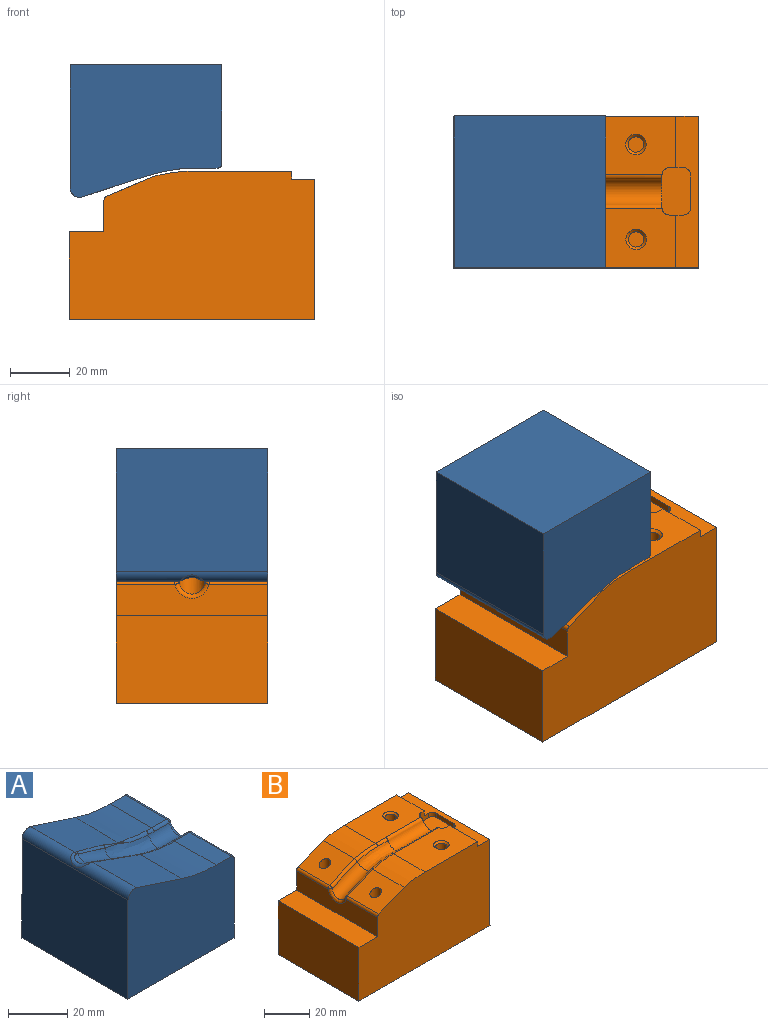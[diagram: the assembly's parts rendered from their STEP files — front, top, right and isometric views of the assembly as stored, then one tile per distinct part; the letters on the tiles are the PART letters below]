
ASSEMBLY  parts=2 mates=1
PART A: 34 faces, bbox 57.8x52.3x48.8 mm
  f0: plane 21.63x21.13mm, normal (0.31,0,0.95), area 465.5mm2, adj f1,f9,f12,f20,f22,f24
  f1: cylinder r=53.34mm len=19.96mm, axis (0,1,0), area 333.5mm2, adj f0,f7,f9,f18,f19
  f2: plane 19.91x7.27mm, normal (0,0,1), area 144.7mm2, adj f6,f10,f13,f29
  f3: plane 50.8x50.8mm, normal (0,0,-1), area 2580.6mm2, adj f4,f8,f9,f10
  f4: plane 50.8x41.16mm, normal (-1,0,0), area 2091mm2, adj f3,f9,f10,f12
  f5: plane 23.15x22.68mm, normal (0.31,0,0.95), area 466.2mm2, adj f6,f10,f12,f28,f30,f32
  f6: cylinder r=53.34mm len=19.99mm, axis (0,1,0), area 334mm2, adj f2,f5,f10,f31,f33
  f7: plane 19.89x7.27mm, normal (0,0,1), area 144.5mm2, adj f1,f9,f14,f21
  f8: plane 50.8x33.27mm, normal (1,0,0), area 1658.3mm2, adj f3,f9,f10,f13,f14,f25
  f9: plane 50.8x44.34mm, normal (0,-1,0), area 1939.6mm2, adj f0,f1,f3,f4,f7,f8,f12,f14
  f10: plane 50.8x44.34mm, normal (0,1,0), area 1939.6mm2, adj f2,f3,f4,f5,f6,f8,f12,f13
  f11: cylinder r=4.52mm len=6.64mm, axis (0.95,0,-0.31), area 18.4mm2, adj f17,f22,f24,f26,f28,f30
  f12: cylinder r=3.17mm len=50.8mm, axis (0,-1,0), area 271.3mm2, adj f0,f4,f5,f9,f10,f26
  f13: cylinder r=1.27mm len=19.91mm, axis (0,-1,0), area 39.7mm2, adj f2,f8,f10,f27
  f14: cylinder r=1.27mm len=19.89mm, axis (0,-1,0), area 39.7mm2, adj f7,f8,f9,f23
  f15: cylinder r=4.52mm len=10.03mm, axis (-1,0,0), area 113.7mm2, adj f16,f19,f21,f25,f29,f31
  f16: bspline ~24x14.71mm, area 247.5mm2, adj f15,f17,f18,f19,f20,f31,f32,f33
  f17: cylinder r=4.52mm len=14.19mm, axis (-0.92,0,0.39), area 124.7mm2, adj f11,f16,f20,f22,f30
  f18: bspline ~18.74x4.92mm, area 22.2mm2, adj f1,f16,f19,f20
  f19: bspline ~7.78x1.25mm, area 4.4mm2, adj f1,f15,f16,f18,f21
  f20: bspline ~12.13x4.67mm, area 11.2mm2, adj f0,f16,f17,f18,f22
  f21: cylinder r=1.27mm len=7.27mm, axis (-1,0,0), area 11.6mm2, adj f7,f15,f19,f23
  f22: bspline ~31.18x10.92mm, area 17.7mm2, adj f0,f11,f17,f20,f24
  f23: sphere r=1.27mm, area 3.1mm2, adj f14,f21,f25
  f24: bspline ~14.81x5.16mm, area 0.9mm2, adj f0,f11,f22,f26
  f25: torus R=5.79mm, axis (1,0,0), area 24.9mm2, adj f8,f15,f23,f27
  f26: bspline ~8.5x4.36mm, area 17.4mm2, adj f11,f12,f24,f28
  f27: sphere r=1.27mm, area 1.2mm2, adj f13,f25,f29
  f28: bspline ~14.81x5.16mm, area 0.9mm2, adj f5,f11,f26,f30
  f29: cylinder r=1.27mm len=7.27mm, axis (-1,0,0), area 11.6mm2, adj f2,f15,f27,f31
  f30: bspline ~13.79x5.13mm, area 17.7mm2, adj f5,f11,f17,f28,f32
  f31: bspline ~7.78x1.25mm, area 4.4mm2, adj f6,f15,f16,f29,f33
  f32: bspline ~9.06x3.7mm, area 5.6mm2, adj f5,f16,f30
  f33: bspline ~16.51x4.08mm, area 22.2mm2, adj f6,f16,f31
PART B: 53 faces, bbox 86.6x55.2x53.9 mm
  f0: cylinder r=50.8mm len=19.81mm, axis (0,-1,0), area 263.6mm2, adj f1,f7,f34,f50
  f1: plane 82.24x49.53mm, normal (0,-1,0), area 3720.5mm2, adj f0,f3,f7,f9,f11,f12,f13,f14
  f2: plane 82.1x49.53mm, normal (0,1,0), area 3713.9mm2, adj f3,f4,f8,f9,f10,f11,f12,f13
  f3: plane 50.82x10.49mm, normal (-1,0,0), area 494.3mm2, adj f1,f2,f14,f43,f46,f47
  f4: cylinder r=50.8mm len=19.8mm, axis (0,-1,0), area 263.5mm2, adj f2,f8,f35,f42
  f5: bspline ~19.41x8.63mm, area 206.2mm2, adj f6,f33,f41,f42,f44,f49,f50,f51
  f6: cylinder r=4.52mm len=16.78mm, axis (-0.92,0,-0.39), area 193.3mm2, adj f5,f44,f47,f49
  f7: plane 33x19.82mm, normal (0,0,1), area 605.9mm2, adj f0,f1,f15,f18,f24,f30,f51,f52
  f8: plane 33x19.82mm, normal (0,0,1), area 604.1mm2, adj f2,f4,f10,f16,f21,f29,f40,f41
  f9: plane 50.82x7.75mm, normal (0,0,1), area 313.1mm2, adj f1,f2,f10,f11,f15,f16,f17,f18
  f10: plane 17.31x2.67mm, normal (1,0,0), area 46.2mm2, adj f2,f8,f9,f16
  f11: plane 50.82x46.87mm, normal (1,0,0), area 2368.9mm2, adj f1,f2,f9,f13,f31
  f12: plane 50.82x29.21mm, normal (-1,0,0), area 1484.5mm2, adj f1,f2,f13,f14
  f13: plane 82.24x50.82mm, normal (0,0,-1), area 4175.9mm2, adj f1,f2,f11,f12
  f14: plane 50.82x11.62mm, normal (0,0,1), area 590.8mm2, adj f1,f2,f3,f12
  f15: plane 17.68x2.67mm, normal (1,0,0), area 47.2mm2, adj f1,f7,f9,f18
  f16: plane 4.99x4.79mm, normal (0,-1,0), area 16.9mm2, adj f8,f9,f10,f20,f21,f22
  f17: plane 11x2.32mm, normal (-1,0,0), area 25.6mm2, adj f9,f20,f22,f23
  f18: plane 4.99x4.79mm, normal (0,1,0), area 16.9mm2, adj f7,f9,f15,f20,f23,f24
  f19: plane 11x4.99mm, normal (1,0,0), area 27mm2, adj f20,f21,f24,f33,f40,f52
  f20: plane 15.83x9.62mm, normal (0,0,1), area 147.2mm2, adj f16,f17,f18,f19,f21,f22,f23,f24
  f21: cylinder r=2.41mm len=4.99mm, axis (0,0,1), area 18.9mm2, adj f8,f16,f19,f20,f40
  f22: cylinder r=2.41mm len=2.41mm, axis (0,0,-1), area 8.8mm2, adj f9,f16,f17,f20
  f23: cylinder r=2.41mm len=2.41mm, axis (0,0,1), area 8.8mm2, adj f9,f17,f18,f20
  f24: cylinder r=2.41mm len=4.99mm, axis (0,0,-1), area 18.9mm2, adj f7,f18,f19,f20,f52
  f25: cylinder r=2.55mm len=18.16mm, axis (0,0,1), area 291.3mm2, adj f26,f30
  f26: plane 5.11x5.11mm, normal (0,0,1), area 20.5mm2, adj f25
  f27: cylinder r=2.55mm len=18.16mm, axis (0,0,1), area 291.3mm2, adj f28,f29
  f28: plane 5.11x5.11mm, normal (0,0,1), area 20.5mm2, adj f27
  f29: cone r=2.55mm half-angle=45deg, axis (0,0,1), area 23.7mm2, adj f8,f27
  f30: cone r=2.55mm half-angle=45deg, axis (0,0,1), area 23.7mm2, adj f7,f25
  f31: cylinder r=2.02mm len=19.06mm, axis (1,0,0), area 241.7mm2, adj f11,f32
  f32: plane 4.04x4.04mm, normal (1,0,0), area 12.8mm2, adj f31
  f33: cylinder r=4.52mm len=21.98mm, axis (-1,0,0), area 243.5mm2, adj f5,f19,f40,f41,f51,f52
  f34: plane 23.98x20.07mm, normal (-0.39,0,0.92), area 313.6mm2, adj f0,f1,f37,f46,f49,f50
  f35: plane 23.98x20.07mm, normal (-0.39,0,0.92), area 313.5mm2, adj f2,f4,f39,f42,f43,f44
  f36: plane 5.11x5.11mm, normal (0,0,1), area 20.5mm2, adj f37
  f37: cylinder r=2.55mm len=21.21mm, axis (0,0,1), area 340.2mm2, adj f34,f36
  f38: plane 5.11x5.11mm, normal (0,0,1), area 20.5mm2, adj f39
  f39: cylinder r=2.55mm len=21.17mm, axis (0,0,1), area 339.6mm2, adj f35,f38
  f40: cylinder r=1.52mm len=22mm, axis (-1,0,0), area 41.1mm2, adj f8,f19,f21,f33,f41
  f41: bspline ~12.12x1.56mm, area 11.7mm2, adj f5,f8,f33,f40,f42
  f42: bspline ~18.43x3.09mm, area 24.8mm2, adj f4,f5,f35,f41,f44
  f43: cylinder r=1.52mm len=19.64mm, axis (0,1,0), area 35mm2, adj f2,f3,f35,f45
  f44: cylinder r=1.52mm len=16.15mm, axis (-0.92,0,-0.39), area 32.9mm2, adj f5,f6,f35,f42,f45
  f45: sphere r=1.52mm, area 1.7mm2, adj f43,f44,f47
  f46: cylinder r=1.52mm len=19.65mm, axis (0,1,0), area 35mm2, adj f1,f3,f34,f48
  f47: bspline ~11.53x5.01mm, area 26.5mm2, adj f3,f6,f45,f48
  f48: sphere r=1.52mm, area 1.7mm2, adj f46,f47,f49
  f49: cylinder r=1.52mm len=16.15mm, axis (-0.92,0,-0.39), area 32.9mm2, adj f5,f6,f34,f48,f50
  f50: bspline ~18.43x3.09mm, area 24.8mm2, adj f0,f5,f34,f49,f51
  f51: bspline ~12.12x1.56mm, area 11.7mm2, adj f5,f7,f33,f50,f52
  f52: cylinder r=1.52mm len=22.03mm, axis (-1,0,0), area 41.1mm2, adj f7,f19,f24,f33,f51
PLACE A rot(axis=(1,0,0),180deg) t=(-40.72,0.11,15.2)mm
PLACE B t=(-41.02,0.12,24.94)mm
MATE cylindrical A.f25 <-> B.f33  axis (1,0,0) through (10.08,0.11,25.46)mm
